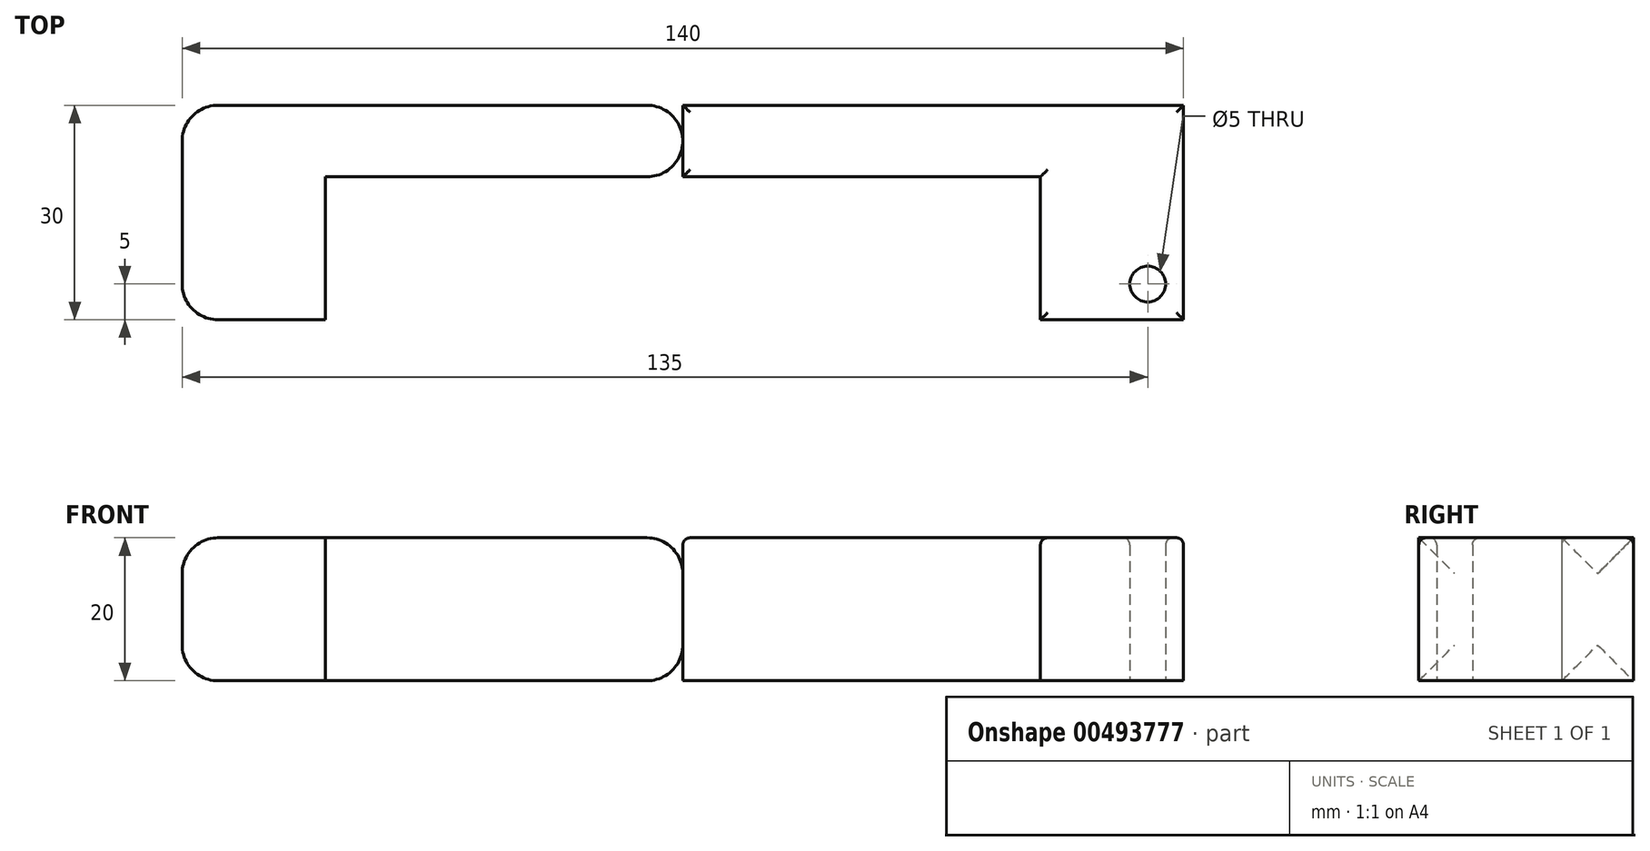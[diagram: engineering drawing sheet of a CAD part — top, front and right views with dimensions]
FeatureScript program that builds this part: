
annotation { "Feature Type Name" : "Feature", "Feature Type Description" : "" }
export const myFeature = defineFeature(function(context is Context, id is Id, definition is map)
    precondition{}
    {
        {
            var Q0;
            Q0=qCreatedBy(makeId("Top.planeOp"),FACE);
            var sketch = newSketch(context, id + "F0", { "sketchPlane" : qUnion([Q0])});
            skLineSegment(sketch, "E0", {"start": v(0, 30) * mm, "end": v(0, 20) * mm});
            skLineSegment(sketch, "E1", {"start": v(0, 20) * mm, "end": v(50, 20) * mm});
            skLineSegment(sketch, "E2", {"start": v(50, 20) * mm, "end": v(50, 0) * mm});
            skLineSegment(sketch, "E3", {"start": v(50, 0) * mm, "end": v(70, 0) * mm});
            skLineSegment(sketch, "E4", {"start": v(70, 0) * mm, "end": v(70, 30) * mm});
            skLineSegment(sketch, "E5", {"start": v(70, 30) * mm, "end": v(0, 30) * mm});
            skSolve(sketch);
        }
        {
            var Q0;
            Q0 = qSketchRegion(id + "F0", true);
            var Q1;
            Q1 = qConstructionFilter(qBodyType(qCreatedBy(id + "F0" ,EDGE), BodyType.WIRE), ConstructionObject.NO);
            extrude(context, id + "F1", {"entities" : qUnion([Q0]), "surfaceEntities" : qUnion([Q1]), "depth" : 20 * mm});
        }
        {
            var Q0;
            Q0=makeQuery(id+"F0.imprint","IMPRINT",FACE,{"disambiguationData":[TD([[makeQuery(id+"F0.imprint","IMPRINT",EDGE,{"derivedFrom":sQuery(id+"F0.wireOp",EDGE,"E0")}),1.0]])]});
            var sketch = newSketch(context, id + "F2", { "sketchPlane" : qUnion([Q0])});
            skPoint(sketch, "E6", {"position": v(65, 5) * mm});
            skSolve(sketch);
        }
        {
            var Q0;
            Q0=makeQuery(id+"F1.opExtrude","SWEPT_BODY",BODY,{"disambiguationData":[OSD([sQuery(id+"F0.wireOp",EDGE,"E5")])]});
            var Q1;
            Q1=qCreatedBy(makeId("Right.planeOp"),FACE);
            mirror(context, id + "F3", {"entities" : qUnion([Q0]), "mirrorPlane" : qUnion([Q1])});
        }
        {
            var Q0;
            Q0=makeQuery(id+"F3.opPattern","COPY",FACE,{"derivedFrom":makeQuery(id+"F1.opExtrude","SWEPT_FACE",FACE,{"disambiguationData":[OSD([sQuery(id+"F0.wireOp",EDGE,"E4")])]}),"instanceName":"1"});
            var Q1;
            Q1=makeQuery(id+"F3.opPattern","COPY",EDGE,{"derivedFrom":makeQuery(id+"F1.opExtrude","SWEPT_EDGE",EDGE,{"disambiguationData":[OSD([sQuery(id+"F0.wireOp",VERTEX,"E2.start")])]}),"instanceName":"1"});
            var Q2;
            Q2=makeQuery(id+"F3.opPattern","COPY",EDGE,{"derivedFrom":makeQuery(id+"F1.opExtrude","SWEPT_EDGE",EDGE,{"disambiguationData":[OSD([sQuery(id+"F0.wireOp",VERTEX,"E5.start")])]}),"instanceName":"1"});
            var Q3;
            Q3=makeQuery(id+"F1.opExtrude","SWEPT_EDGE",EDGE,{"disambiguationData":[OSD([sQuery(id+"F0.wireOp",VERTEX,"E5.end")])]});
            var Q4;
            Q4=makeQuery(id+"F1.opExtrude","SWEPT_EDGE",EDGE,{"disambiguationData":[OSD([sQuery(id+"F0.wireOp",VERTEX,"E4.start")])]});
            var Q5;
            Q5=makeQuery(id+"F1.opExtrude","SWEPT_EDGE",EDGE,{"disambiguationData":[OSD([sQuery(id+"F0.wireOp",VERTEX,"E3.start")])]});
            var Q6;
            Q6=makeQuery(id+"F1.opExtrude","SWEPT_EDGE",EDGE,{"disambiguationData":[OSD([sQuery(id+"F0.wireOp",VERTEX,"E2.start")])]});
            var Q7;
            Q7=makeQuery(id+"F1.opExtrude","SWEPT_EDGE",EDGE,{"disambiguationData":[OSD([sQuery(id+"F0.wireOp",VERTEX,"E1.start")])]});
            var Q8;
            Q8=makeQuery(id+"F3.opPattern","COPY",EDGE,{"derivedFrom":makeQuery(id+"F1.opExtrude","SWEPT_EDGE",EDGE,{"disambiguationData":[OSD([sQuery(id+"F0.wireOp",VERTEX,"E1.start")])]}),"instanceName":"1"});
            var Q9;
            Q9=makeQuery(id+"F3.opPattern","COPY",EDGE,{"derivedFrom":makeQuery(id+"F1.opExtrude","SWEPT_EDGE",EDGE,{"disambiguationData":[OSD([sQuery(id+"F0.wireOp",VERTEX,"E5.end")])]}),"instanceName":"1"});
            var Q10;
            Q10=makeQuery(id+"F3.opPattern","COPY",EDGE,{"derivedFrom":makeQuery(id+"F1.opExtrude","SWEPT_EDGE",EDGE,{"disambiguationData":[OSD([sQuery(id+"F0.wireOp",VERTEX,"E3.start")])]}),"instanceName":"1"});
            var Q11;
            Q11=makeQuery(id+"F3.opPattern","COPY",EDGE,{"derivedFrom":makeQuery(id+"F1.opExtrude","SWEPT_EDGE",EDGE,{"disambiguationData":[OSD([sQuery(id+"F0.wireOp",VERTEX,"E4.start")])]}),"instanceName":"1"});
            var Q12;
            Q12=makeQuery(id+"F1.opExtrude","SWEPT_EDGE",EDGE,{"disambiguationData":[OSD([sQuery(id+"F0.wireOp",VERTEX,"E5.start")])]});
            fillet(context, id + "F4", {"entities" : qUnion([Q0, Q1, Q2, Q3, Q4, Q5, Q6, Q7, Q8, Q9, Q10, Q11, Q12]), "radius" : 5 * mm, "tangentPropagation" : true, "allowEdgeOverflow" : false});
        }
        {
            var Q0;
            Q0=sQuery(id+"F2.wireOp",VERTEX,"E6");
            var Q1;
            Q1=makeQuery(id+"F1.opExtrude","SWEPT_BODY",BODY,{"disambiguationData":[OSD([sQuery(id+"F0.wireOp",EDGE,"E0"),sQuery(id+"F0.wireOp",EDGE,"E1"),sQuery(id+"F0.wireOp",EDGE,"E2"),sQuery(id+"F0.wireOp",EDGE,"E3"),sQuery(id+"F0.wireOp",EDGE,"E4"),sQuery(id+"F0.wireOp",EDGE,"E5")])]});
            hole(context, id + "F5", {"style" : HoleStyle.SIMPLE, "endStyle" : HoleEndStyle.THROUGH, "oppositeDirection" : true, "holeDiameter" : 5 * mm, "isTappedThrough" : true, "tappedDepth" : 12 * mm, "tapClearance" : 3, "locations" : qUnion([Q0]), "scope" : qUnion([Q1])});
        }
        {
            var Q0;
            Q0=makeQuery(id+"F1.opExtrude","CAP_EDGE",EDGE,{"disambiguationData":[OSD([sQuery(id+"F0.wireOp",EDGE,"E3")])],"isStart":true});
            var Q1;
            Q1=makeQuery(id+"F5.hole-0.boolean.opBoolean","INTERSECT",EDGE,{"derivedFrom":[makeQuery(id+"F1.opExtrude","CAP_FACE",FACE,{"disambiguationData":[OSD([sQuery(id+"F0.wireOp",EDGE,"E0"),sQuery(id+"F0.wireOp",EDGE,"E1"),sQuery(id+"F0.wireOp",EDGE,"E2"),sQuery(id+"F0.wireOp",EDGE,"E3"),sQuery(id+"F0.wireOp",EDGE,"E4"),sQuery(id+"F0.wireOp",EDGE,"E5")])],"isStart":false}),makeQuery(id+"F5.hole-0.opRevolve","SWEPT_FACE",FACE,{"disambiguationData":[OSD([sQuery(id+"F5.hole-0.sketch.wireOp",EDGE,"core_line_2")])]})]});
            var Q2;
            Q2=makeQuery(id+"F1.opExtrude","CAP_EDGE",EDGE,{"disambiguationData":[OSD([sQuery(id+"F0.wireOp",EDGE,"E5")])],"isStart":false});
            var Q3;
            Q3=makeQuery(id+"F1.opExtrude","SWEPT_EDGE",EDGE,{"disambiguationData":[OSD([sQuery(id+"F0.wireOp",EDGE,"E0"),sQuery(id+"F0.wireOp",EDGE,"E5")])]});
            var Q4;
            Q4=makeQuery(id+"F1.opExtrude","CAP_EDGE",EDGE,{"disambiguationData":[OSD([sQuery(id+"F0.wireOp",EDGE,"E0")])],"isStart":false});
            var Q5;
            Q5=makeQuery(id+"F5.hole-0.boolean.opBoolean","COPY",EDGE,{"derivedFrom":makeQuery(id+"F5.hole-0.opRevolve","SWEPT_EDGE",EDGE,{"disambiguationData":[OSD([sQuery(id+"F5.hole-0.sketch.wireOp",EDGE,"core_line_2"),sQuery(id+"F5.hole-0.sketch.wireOp",EDGE,"core_line_3")])]})});
            var Q6;
            Q6=makeQuery(id+"F3.opPattern","COPY",EDGE,{"derivedFrom":makeQuery(id+"F1.opExtrude","SWEPT_EDGE",EDGE,{"disambiguationData":[OSD([sQuery(id+"F0.wireOp",EDGE,"E0"),sQuery(id+"F0.wireOp",EDGE,"E5")])]}),"instanceName":"1"});
            var Q7;
            Q7=makeQuery(id+"F3.opPattern","COPY",EDGE,{"derivedFrom":makeQuery(id+"F1.opExtrude","CAP_EDGE",EDGE,{"disambiguationData":[OSD([sQuery(id+"F0.wireOp",EDGE,"E0")])],"isStart":false}),"instanceName":"1"});
            var Q8;
            Q8=makeQuery(id+"F1.opExtrude","CAP_EDGE",EDGE,{"disambiguationData":[OSD([sQuery(id+"F0.wireOp",EDGE,"E5")])],"isStart":true});
            var Q9;
            Q9=makeQuery(id+"F1.opExtrude","CAP_EDGE",EDGE,{"disambiguationData":[OSD([sQuery(id+"F0.wireOp",EDGE,"E1")])],"isStart":true});
            var Q10;
            Q10=makeQuery(id+"F1.opExtrude","CAP_EDGE",EDGE,{"disambiguationData":[OSD([sQuery(id+"F0.wireOp",EDGE,"E3")])],"isStart":false});
            var Q11;
            Q11=makeQuery(id+"F1.opExtrude","CAP_EDGE",EDGE,{"disambiguationData":[OSD([sQuery(id+"F0.wireOp",EDGE,"E0")])],"isStart":true});
            var Q12;
            Q12=makeQuery(id+"F1.opExtrude","CAP_EDGE",EDGE,{"disambiguationData":[OSD([sQuery(id+"F0.wireOp",EDGE,"E2")])],"isStart":true});
            var Q13;
            Q13=makeQuery(id+"F1.opExtrude","SWEPT_EDGE",EDGE,{"disambiguationData":[OSD([sQuery(id+"F0.wireOp",EDGE,"E1"),sQuery(id+"F0.wireOp",EDGE,"E2")])]});
            var Q14;
            Q14=makeQuery(id+"F1.opExtrude","CAP_EDGE",EDGE,{"disambiguationData":[OSD([sQuery(id+"F0.wireOp",EDGE,"E1")])],"isStart":false});
            var Q15;
            Q15=makeQuery(id+"F1.opExtrude","CAP_EDGE",EDGE,{"disambiguationData":[OSD([sQuery(id+"F0.wireOp",EDGE,"E2")])],"isStart":false});
            var Q16;
            Q16=makeQuery(id+"F1.opExtrude","SWEPT_EDGE",EDGE,{"disambiguationData":[OSD([sQuery(id+"F0.wireOp",EDGE,"E2"),sQuery(id+"F0.wireOp",EDGE,"E3")])]});
            var Q17;
            Q17=makeQuery(id+"F1.opExtrude","CAP_EDGE",EDGE,{"disambiguationData":[OSD([sQuery(id+"F0.wireOp",EDGE,"E4")])],"isStart":false});
            var Q18;
            Q18=makeQuery(id+"F1.opExtrude","CAP_EDGE",EDGE,{"disambiguationData":[OSD([sQuery(id+"F0.wireOp",EDGE,"E4")])],"isStart":true});
            var Q19;
            Q19=makeQuery(id+"F1.opExtrude","SWEPT_EDGE",EDGE,{"disambiguationData":[OSD([sQuery(id+"F0.wireOp",EDGE,"E4"),sQuery(id+"F0.wireOp",EDGE,"E5")])]});
            var Q20;
            Q20=makeQuery(id+"F3.opPattern","COPY",EDGE,{"derivedFrom":makeQuery(id+"F1.opExtrude","CAP_EDGE",EDGE,{"disambiguationData":[OSD([sQuery(id+"F0.wireOp",EDGE,"E0")])],"isStart":true}),"instanceName":"1"});
            var Q21;
            Q21=makeQuery(id+"F1.opExtrude","SWEPT_EDGE",EDGE,{"disambiguationData":[OSD([sQuery(id+"F0.wireOp",EDGE,"E0"),sQuery(id+"F0.wireOp",EDGE,"E1")])]});
            var Q22;
            Q22=makeQuery(id+"F1.opExtrude","SWEPT_EDGE",EDGE,{"disambiguationData":[OSD([sQuery(id+"F0.wireOp",EDGE,"E3"),sQuery(id+"F0.wireOp",EDGE,"E4")])]});
            var Q23;
            Q23=makeQuery(id+"F3.opPattern","COPY",EDGE,{"derivedFrom":makeQuery(id+"F1.opExtrude","SWEPT_EDGE",EDGE,{"disambiguationData":[OSD([sQuery(id+"F0.wireOp",EDGE,"E0"),sQuery(id+"F0.wireOp",EDGE,"E1")])]}),"instanceName":"1"});
            fillet(context, id + "F6", {"entities" : qUnion([Q0, Q1, Q2, Q3, Q4, Q5, Q6, Q7, Q8, Q9, Q10, Q11, Q12, Q13, Q14, Q15, Q16, Q17, Q18, Q19, Q20, Q21, Q22, Q23]), "radius" : 5 * mm, "tangentPropagation" : true, "allowEdgeOverflow" : false});
        }
        {
            var Q0;
            Q0=makeQuery(id+"F5.hole-0.boolean.opBoolean","INTERSECT",EDGE,{"derivedFrom":[makeQuery(id+"F1.opExtrude","CAP_FACE",FACE,{"disambiguationData":[OSD([sQuery(id+"F0.wireOp",EDGE,"E0"),sQuery(id+"F0.wireOp",EDGE,"E1"),sQuery(id+"F0.wireOp",EDGE,"E2"),sQuery(id+"F0.wireOp",EDGE,"E3"),sQuery(id+"F0.wireOp",EDGE,"E4"),sQuery(id+"F0.wireOp",EDGE,"E5")])],"isStart":false}),makeQuery(id+"F5.hole-0.opRevolve","SWEPT_FACE",FACE,{"disambiguationData":[OSD([sQuery(id+"F5.hole-0.sketch.wireOp",EDGE,"core_line_2")])]})]});
            var Q1;
            Q1=makeQuery(id+"F5.hole-0.boolean.opBoolean","COPY",EDGE,{"derivedFrom":makeQuery(id+"F5.hole-0.opRevolve","SWEPT_EDGE",EDGE,{"disambiguationData":[OSD([sQuery(id+"F5.hole-0.sketch.wireOp",EDGE,"core_line_2"),sQuery(id+"F5.hole-0.sketch.wireOp",EDGE,"core_line_3")])]})});
            var Q2;
            Q2=makeQuery(id+"F1.opExtrude","CAP_FACE",FACE,{"disambiguationData":[OSD([sQuery(id+"F0.wireOp",EDGE,"E0"),sQuery(id+"F0.wireOp",EDGE,"E1"),sQuery(id+"F0.wireOp",EDGE,"E2"),sQuery(id+"F0.wireOp",EDGE,"E3"),sQuery(id+"F0.wireOp",EDGE,"E4"),sQuery(id+"F0.wireOp",EDGE,"E5")])],"isStart":false});
            fillet(context, id + "F7", {"entities" : qUnion([Q0, Q1, Q2]), "radius" : 1 * mm, "tangentPropagation" : true, "allowEdgeOverflow" : false});
        }
    });
